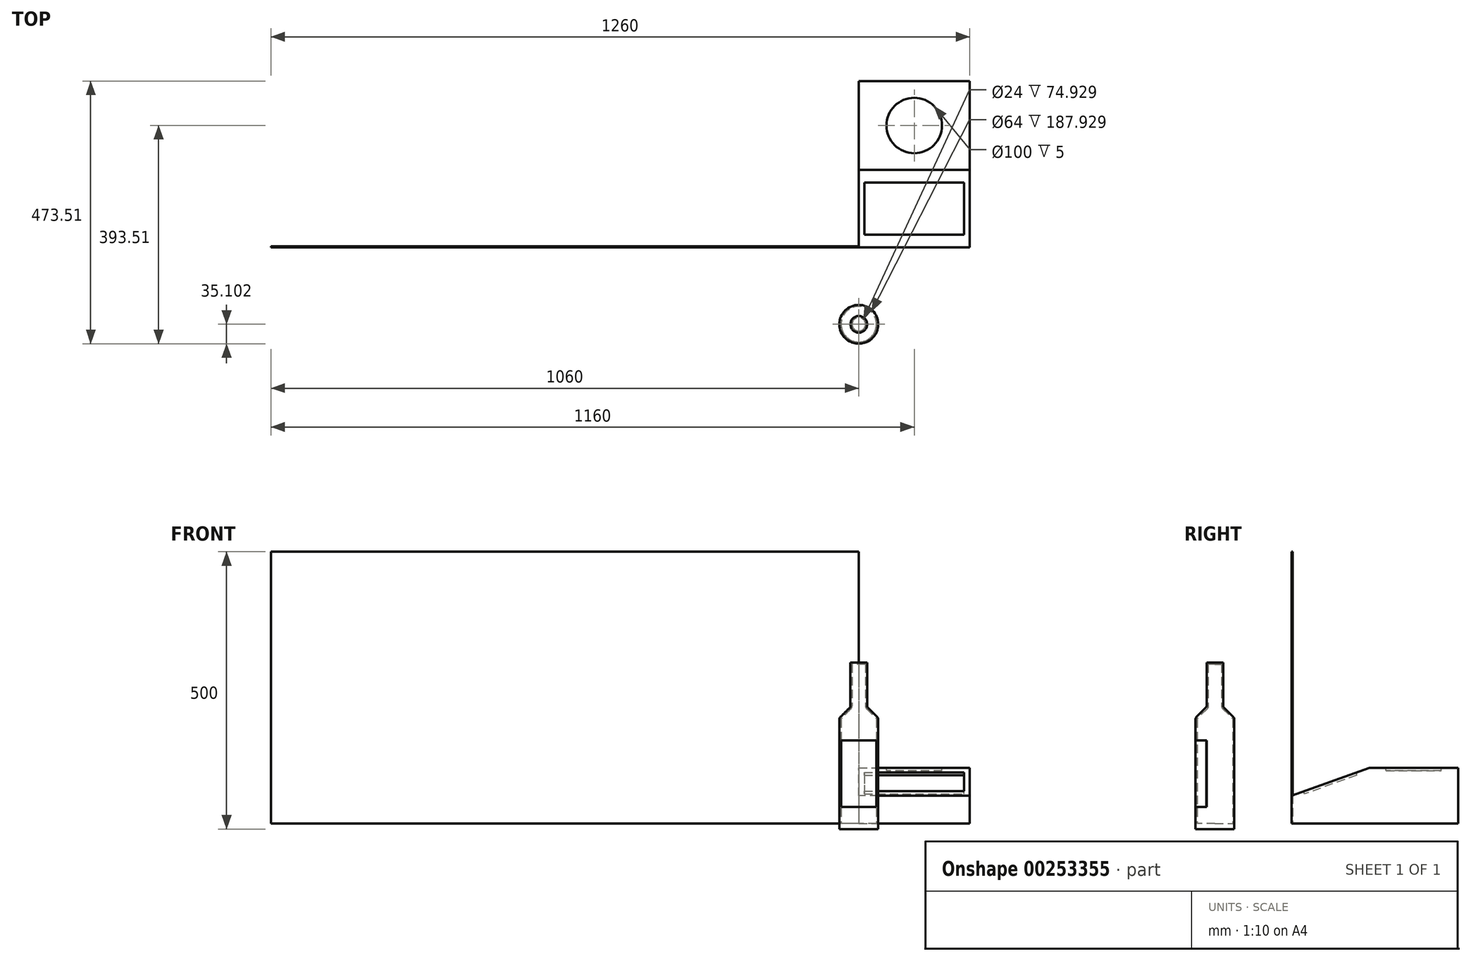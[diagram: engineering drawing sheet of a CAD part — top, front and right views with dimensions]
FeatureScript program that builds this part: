
annotation { "Feature Type Name" : "Feature", "Feature Type Description" : "" }
export const myFeature = defineFeature(function(context is Context, id is Id, definition is map)
    precondition{}
    {
        {
            var Q0;
            Q0=qCreatedBy(makeId("Top.planeOp"),FACE);
            var sketch = newSketch(context, id + "F0", { "sketchPlane" : qUnion([Q0])});
            skLineSegment(sketch, "E0.bottom", {"start": v(0, 0) * mm, "end": v(200, 0) * mm});
            skLineSegment(sketch, "E0.top", {"start": v(0, 300) * mm, "end": v(200, 300) * mm});
            skLineSegment(sketch, "E0.left", {"start": v(0, 0) * mm, "end": v(0, 300) * mm});
            skLineSegment(sketch, "E0.right", {"start": v(200, 0) * mm, "end": v(200, 300) * mm});
            skLineSegment(sketch, "E1.bottom", {"start": v(0, 0) * mm, "end": v(-1060, 0) * mm});
            skLineSegment(sketch, "E1.top", {"start": v(0, 2) * mm, "end": v(-1060, 2) * mm});
            skLineSegment(sketch, "E1.left", {"start": v(0, 0) * mm, "end": v(0, 2) * mm});
            skLineSegment(sketch, "E1.right", {"start": v(-1060, 0) * mm, "end": v(-1060, 2) * mm});
            skCircle(sketch, "E2", {"center": v(0, -138.4) * mm, "radius": 15 * mm});
            skCircle(sketch, "E3", {"center": v(0, -138.4) * mm, "radius": 12 * mm});
            skCircle(sketch, "E4", {"center": v(0, -138.4) * mm, "radius": 32 * mm});
            skCircle(sketch, "E5", {"center": v(0, -138.4) * mm, "radius": 35 * mm});
            skCircle(sketch, "E6", {"center": v(0, -138.4) * mm, "radius": 35.1 * mm});
            skLineSegment(sketch, "E7", {"start": v(-31.9, -153.05) * mm, "end": v(-31.8, -153.05) * mm});
            skLineSegment(sketch, "E8", {"start": v(31.6, -153.46) * mm, "end": v(31.67, -153.53) * mm});
            skSolve(sketch);
        }
        {
            var Q0;
            Q0=makeQuery(id+"F0.imprint","IMPRINT",FACE,{"disambiguationData":[TD([[makeQuery(id+"F0.imprint","IMPRINT",EDGE,{"derivedFrom":sQuery(id+"F0.wireOp",EDGE,"E0.bottom")}),1.0]])]});
            extrude(context, id + "F1", {"entities" : qUnion([Q0]), "depth" : 100 * mm});
        }
        {
            var Q0;
            Q0=makeQuery(id+"F1.opExtrude","CAP_FACE",FACE,{"disambiguationData":[OSD([sQuery(id+"F0.wireOp",EDGE,"E0.bottom"),sQuery(id+"F0.wireOp",EDGE,"E0.top"),sQuery(id+"F0.wireOp",EDGE,"E0.left"),sQuery(id+"F0.wireOp",EDGE,"E0.right")])],"isStart":false});
            var sketch = newSketch(context, id + "F2", { "sketchPlane" : qUnion([Q0])});
            skLineSegment(sketch, "E9", {"start": v(100, 300) * mm, "end": v(100, 0) * mm});
            skCircle(sketch, "E10", {"center": v(100, 220) * mm, "radius": 50 * mm});
            skSolve(sketch);
        }
        {
            var Q0;
            Q0=makeQuery(id+"F1.opExtrude","CAP_EDGE",EDGE,{"disambiguationData":[OSD([sQuery(id+"F0.wireOp",EDGE,"E0.bottom")])],"isStart":false});
            chamfer(context, id + "F3", {"entities" : qUnion([Q0]), "chamferType" : ChamferType.TWO_OFFSETS, "width1" : 140 * mm, "oppositeDirection" : false, "width2" : 50 * mm, "tangentPropagation" : true});
        }
        {
            var Q0;
            Q0=makeQuery(id+"F3.opChamfer","BLEND_FACE",FACE,{"disambiguationData":[OSD([sQuery(id+"F0.wireOp",EDGE,"E0.bottom")])]});
            var sketch = newSketch(context, id + "F4", { "sketchPlane" : qUnion([Q0])});
            skLineSegment(sketch, "E11.0", {"start": v(0, 165.48) * mm, "end": v(200, 165.48) * mm});
            skLineSegment(sketch, "E11.1", {"start": v(200, 16.82) * mm, "end": v(0, 16.82) * mm});
            skLineSegment(sketch, "E11.2", {"start": v(200, 165.48) * mm, "end": v(200, 16.82) * mm});
            skLineSegment(sketch, "E11.3", {"start": v(0, 16.82) * mm, "end": v(0, 165.48) * mm});
            skLineSegment(sketch, "E12.bottom", {"start": v(10, 141.15) * mm, "end": v(190, 141.15) * mm});
            skLineSegment(sketch, "E12.top", {"start": v(10, 41.15) * mm, "end": v(190, 41.15) * mm});
            skLineSegment(sketch, "E12.left", {"start": v(10, 141.15) * mm, "end": v(10, 41.15) * mm});
            skLineSegment(sketch, "E12.right", {"start": v(190, 141.15) * mm, "end": v(190, 41.15) * mm});
            skPoint(sketch, "E12.middle", {"position": v(100, 91.15) * mm});
            skPoint(sketch, "E12.middle.positionSnap0", {"position": v(200, 91.15) * mm});
            skPoint(sketch, "E12.middle.positionSnap1", {"position": v(100, 16.82) * mm});
            skPoint(sketch, "E12.centerSnap0", {"position": v(200, 91.15) * mm});
            skPoint(sketch, "E12.centerSnap1", {"position": v(100, 16.82) * mm});
            skSolve(sketch);
        }
        {
            var Q0;
            {var subQ0=sQuery(id+"F2.wireOp",EDGE,"E10");var subQ1=sQuery(id+"F2.wireOp",EDGE,"E9");var subQ2=makeQuery(id+"F2.imprint","INTERSECT",VERTEX,{"disambiguationData":[OD(0.0)],"derivedFrom":[subQ1,subQ0]});Q0=makeQuery(id+"F2.imprint","IMPRINT",FACE,{"disambiguationData":[TD([[makeQuery(id+"F2.imprint","IMPRINT",EDGE,{"disambiguationData":[TD([[subQ2,-1.0]])],"derivedFrom":subQ1}),-1.0]])]});}
            var Q1;
            {var subQ0=sQuery(id+"F2.wireOp",EDGE,"E10");var subQ1=sQuery(id+"F2.wireOp",EDGE,"E9");var subQ2=makeQuery(id+"F2.imprint","INTERSECT",VERTEX,{"disambiguationData":[OD(0.0)],"derivedFrom":[subQ1,subQ0]});Q1=makeQuery(id+"F2.imprint","IMPRINT",FACE,{"disambiguationData":[TD([[makeQuery(id+"F2.imprint","IMPRINT",EDGE,{"disambiguationData":[TD([[subQ2,-1.0]])],"derivedFrom":subQ1}),1.0]])]});}
            var Q2;
            Q2=makeQuery(id+"F4.imprint","IMPRINT",FACE,{"disambiguationData":[TD([[makeQuery(id+"F4.imprint","IMPRINT",EDGE,{"derivedFrom":sQuery(id+"F4.wireOp",EDGE,"E12.bottom")}),-1.0]])]});
            extrude(context, id + "F5", {"entities" : qUnion([Q0, Q1, Q2]), "operationType" : NewBodyOperationType.REMOVE, "oppositeDirection" : true, "depth" : 5 * mm});
        }
        {
            var Q0;
            Q0=makeQuery(id+"F0.imprint","IMPRINT",FACE,{"disambiguationData":[TD([[makeQuery(id+"F0.imprint","IMPRINT",EDGE,{"derivedFrom":sQuery(id+"F0.wireOp",EDGE,"E1.bottom")}),-1.0]])]});
            extrude(context, id + "F6", {"entities" : qUnion([Q0]), "depth" : 490 * mm});
        }
        {
            var Q0;
            Q0=makeQuery(id+"F0.imprint","IMPRINT",FACE,{"disambiguationData":[TD([[makeQuery(id+"F0.imprint","IMPRINT",EDGE,{"derivedFrom":sQuery(id+"F0.wireOp",EDGE,"E3")}),1.0]])]});
            var Q1;
            Q1=makeQuery(id+"F0.imprint","IMPRINT",FACE,{"disambiguationData":[TD([[makeQuery(id+"F0.imprint","IMPRINT",EDGE,{"derivedFrom":sQuery(id+"F0.wireOp",EDGE,"E2")}),1.0]])]});
            var Q2;
            Q2=makeQuery(id+"F0.imprint","IMPRINT",FACE,{"disambiguationData":[TD([[makeQuery(id+"F0.imprint","IMPRINT",EDGE,{"derivedFrom":sQuery(id+"F0.wireOp",EDGE,"E2")}),-1.0]])]});
            var Q3;
            Q3=makeQuery(id+"F0.imprint","IMPRINT",FACE,{"disambiguationData":[TD([[makeQuery(id+"F0.imprint","IMPRINT",EDGE,{"derivedFrom":sQuery(id+"F0.wireOp",EDGE,"E4")}),-1.0]])]});
            extrude(context, id + "F7", {"entities" : qUnion([Q0, Q1, Q2, Q3]), "depth" : 210 * mm});
        }
        {
            var Q0;
            Q0=makeQuery(id+"F0.imprint","IMPRINT",FACE,{"disambiguationData":[TD([[makeQuery(id+"F0.imprint","IMPRINT",EDGE,{"derivedFrom":sQuery(id+"F0.wireOp",EDGE,"E3")}),1.0]])]});
            var Q1;
            Q1=makeQuery(id+"F0.imprint","IMPRINT",FACE,{"disambiguationData":[TD([[makeQuery(id+"F0.imprint","IMPRINT",EDGE,{"derivedFrom":sQuery(id+"F0.wireOp",EDGE,"E2")}),1.0]])]});
            extrude(context, id + "F8", {"entities" : qUnion([Q0, Q1]), "operationType" : NewBodyOperationType.ADD, "depth" : 290 * mm});
        }
        {
            var Q0;
            Q0=makeQuery(id+"F7.opExtrude","CAP_EDGE",EDGE,{"disambiguationData":[OSD([sQuery(id+"F0.wireOp",EDGE,"E5")])],"isStart":false});
            chamfer(context, id + "F9", {"entities" : qUnion([Q0]), "chamferType" : ChamferType.OFFSET_ANGLE, "width" : 20 * mm, "oppositeDirection" : false, "angle" : 45 * degree, "tangentPropagation" : true});
        }
        {
            var Q0;
            Q0=makeQuery(id+"F9.opChamfer","BLEND_EDGE",EDGE,{"blendedFrom":[makeQuery(id+"F7.opExtrude","CAP_EDGE",EDGE,{"disambiguationData":[OSD([sQuery(id+"F0.wireOp",EDGE,"E5")])],"isStart":false}),makeQuery(id+"F8.opExtrude","SWEPT_FACE",FACE,{"disambiguationData":[OSD([sQuery(id+"F0.wireOp",EDGE,"E2")])]})],"blendedInto":[makeQuery(id+"F8.opExtrude","SWEPT_FACE",FACE,{"disambiguationData":[OSD([sQuery(id+"F0.wireOp",EDGE,"E2")])]})]});
            var Q1;
            {var subQ0=sQuery(id+"F0.wireOp",EDGE,"E5");Q1=makeQuery(id+"F9.opChamfer","BLEND_EDGE",EDGE,{"blendedFrom":[makeQuery(id+"F7.opExtrude","CAP_EDGE",EDGE,{"disambiguationData":[OSD([subQ0])],"isStart":false}),makeQuery(id+"F7.opExtrude","SWEPT_FACE",FACE,{"disambiguationData":[OSD([subQ0])]})],"blendedInto":[makeQuery(id+"F7.opExtrude","SWEPT_FACE",FACE,{"disambiguationData":[OSD([subQ0])]})]});}
            fillet(context, id + "F10", {"entities" : qUnion([Q0, Q1]), "radius" : 5 * mm, "tangentPropagation" : true, "allowEdgeOverflow" : false});
        }
        {
            var Q0;
            Q0=makeQuery(id+"F7.opExtrude","CAP_FACE",FACE,{"disambiguationData":[OSD([sQuery(id+"F0.wireOp",EDGE,"E5")])],"isStart":true});
            shell(context, id + "F11", {"entities" : qUnion([Q0]), "thickness" : 3 * mm});
        }
        {
            var Q0;
            Q0=makeQuery(id+"F0.imprint","IMPRINT",FACE,{"disambiguationData":[TD([[makeQuery(id+"F0.imprint","IMPRINT",EDGE,{"derivedFrom":sQuery(id+"F0.wireOp",EDGE,"E3")}),1.0]])]});
            var Q1;
            Q1=makeQuery(id+"F0.imprint","IMPRINT",FACE,{"disambiguationData":[TD([[makeQuery(id+"F0.imprint","IMPRINT",EDGE,{"derivedFrom":sQuery(id+"F0.wireOp",EDGE,"E2")}),1.0]])]});
            var Q2;
            Q2=makeQuery(id+"F0.imprint","IMPRINT",FACE,{"disambiguationData":[TD([[makeQuery(id+"F0.imprint","IMPRINT",EDGE,{"derivedFrom":sQuery(id+"F0.wireOp",EDGE,"E2")}),-1.0]])]});
            var Q3;
            Q3=makeQuery(id+"F0.imprint","IMPRINT",FACE,{"disambiguationData":[TD([[makeQuery(id+"F0.imprint","IMPRINT",EDGE,{"derivedFrom":sQuery(id+"F0.wireOp",EDGE,"E4")}),-1.0]])]});
            extrude(context, id + "F12", {"entities" : qUnion([Q0, Q1, Q2, Q3]), "operationType" : NewBodyOperationType.ADD, "oppositeDirection" : true, "depth" : 10 * mm});
        }
        {
            var Q0;
            {var subQ0=sQuery(id+"F0.wireOp",EDGE,"E7");Q0=makeQuery(id+"F0.imprint","IMPRINT",FACE,{"disambiguationData":[TD([[makeQuery(id+"F0.imprint","IMPRINT",EDGE,{"derivedFrom":subQ0}),-1.0]])]});}
            extrude(context, id + "F13", {"entities" : qUnion([Q0]), "depth" : 150 * mm, "hasSecondDirection" : true, "secondDirectionOppositeDirection" : false, "secondDirectionDepth" : 30 * mm});
        }
    });
